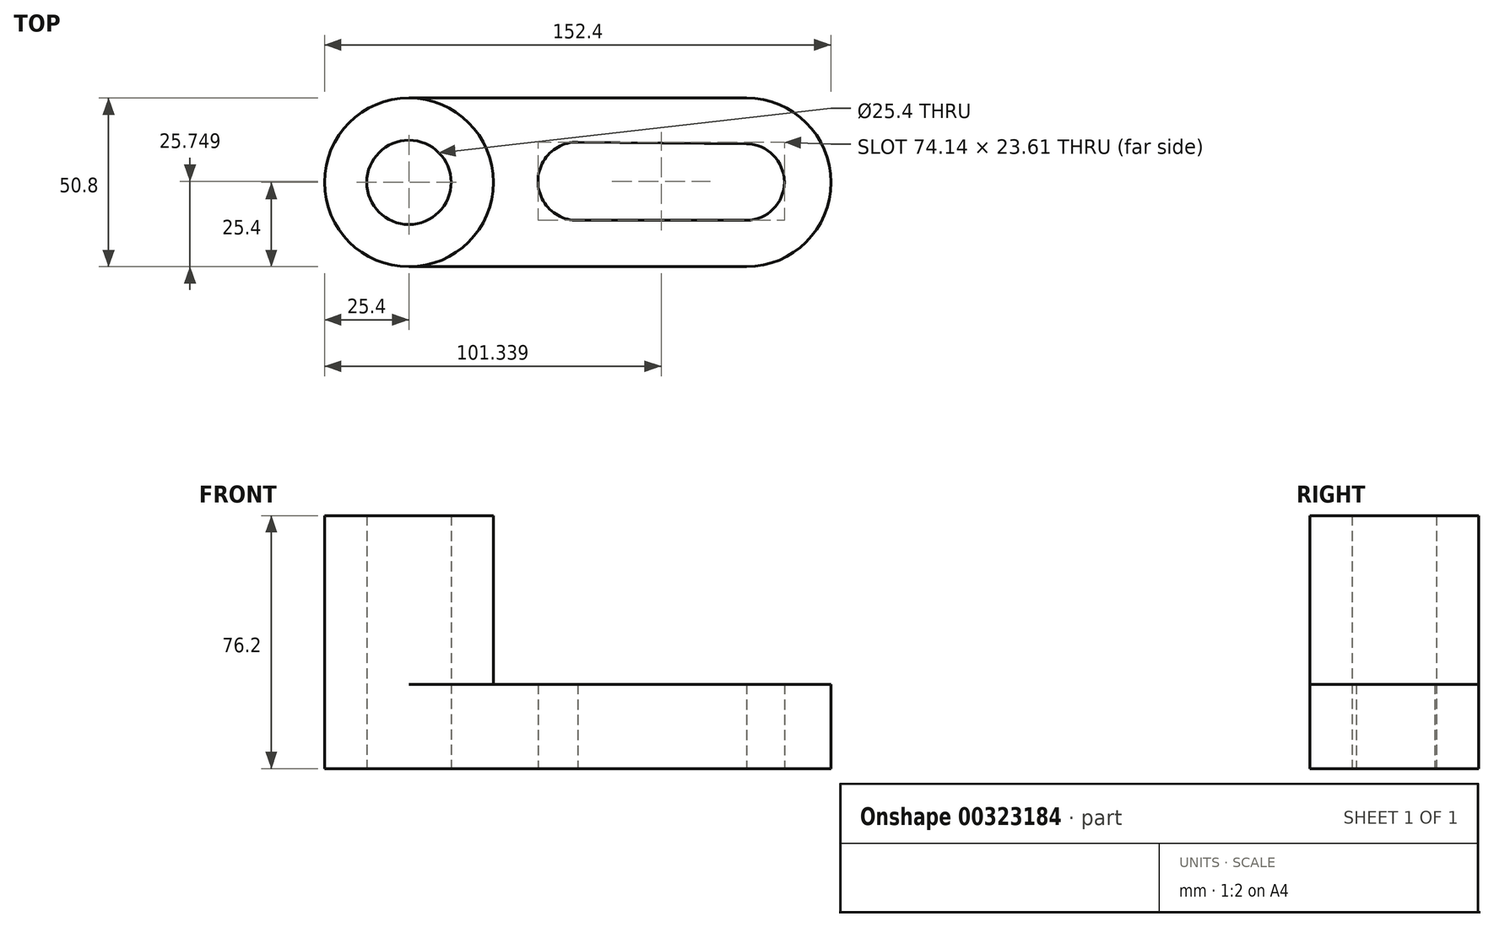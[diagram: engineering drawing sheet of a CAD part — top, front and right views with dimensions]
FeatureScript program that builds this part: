
annotation { "Feature Type Name" : "Feature", "Feature Type Description" : "" }
export const myFeature = defineFeature(function(context is Context, id is Id, definition is map)
    precondition{}
    {
        {
            var Q0;
            Q0=qCreatedBy(makeId("Top.planeOp"),FACE);
            var sketch = newSketch(context, id + "F0", { "sketchPlane" : qUnion([Q0])});
            skLineSegment(sketch, "E0", {"start": v(-47.55, 44.6) * mm, "end": v(54.05, 44.6) * mm});
            skLineSegment(sketch, "E1", {"start": v(-47.55, -6.2) * mm, "end": v(54.05, -6.2) * mm});
            skArc(sketch, "E2", {"start": v(54.05, 44.6) * mm, "mid": v(79.45, 19.2) * mm, "end": v(54.05, -6.2) * mm});
            skCircle(sketch, "E3", {"center": v(-47.55, 19.2) * mm, "radius": 25.4 * mm});
            skCircle(sketch, "E4", {"center": v(-47.55, 19.2) * mm, "radius": 12.7 * mm});
            skLineSegment(sketch, "E5", {"start": v(54.05, 30.8) * mm, "end": v(3.25, 31.34) * mm});
            skLineSegment(sketch, "E6", {"start": v(54.05, 7.73) * mm, "end": v(3.25, 7.73) * mm});
            skArc(sketch, "E7", {"start": v(54.05, 30.8) * mm, "mid": v(65.46, 19.27) * mm, "end": v(54.05, 7.73) * mm});
            skArc(sketch, "E8", {"start": v(3.25, 31.34) * mm, "mid": v(-8.68, 19.54) * mm, "end": v(3.25, 7.73) * mm});
            skSolve(sketch);
        }
        {
            var Q0;
            {var subQ1=sQuery(id+"F0.wireOp",EDGE,"E0");Q0=makeQuery(id+"F0.imprint","IMPRINT",FACE,{"disambiguationData":[TD([[makeQuery(id+"F0.imprint","IMPRINT",EDGE,{"derivedFrom":subQ1}),-1.0]])]});}
            extrude(context, id + "F1", {"entities" : qUnion([Q0]), "depth" : 25.4 * mm});
        }
        {
            var Q0;
            Q0=makeQuery(id+"F0.imprint","IMPRINT",FACE,{"disambiguationData":[TD([[makeQuery(id+"F0.imprint","IMPRINT",EDGE,{"derivedFrom":sQuery(id+"F0.wireOp",EDGE,"E4")}),-1.0]])]});
            extrude(context, id + "F2", {"entities" : qUnion([Q0]), "operationType" : NewBodyOperationType.ADD, "depth" : 76.2 * mm});
        }
    });
